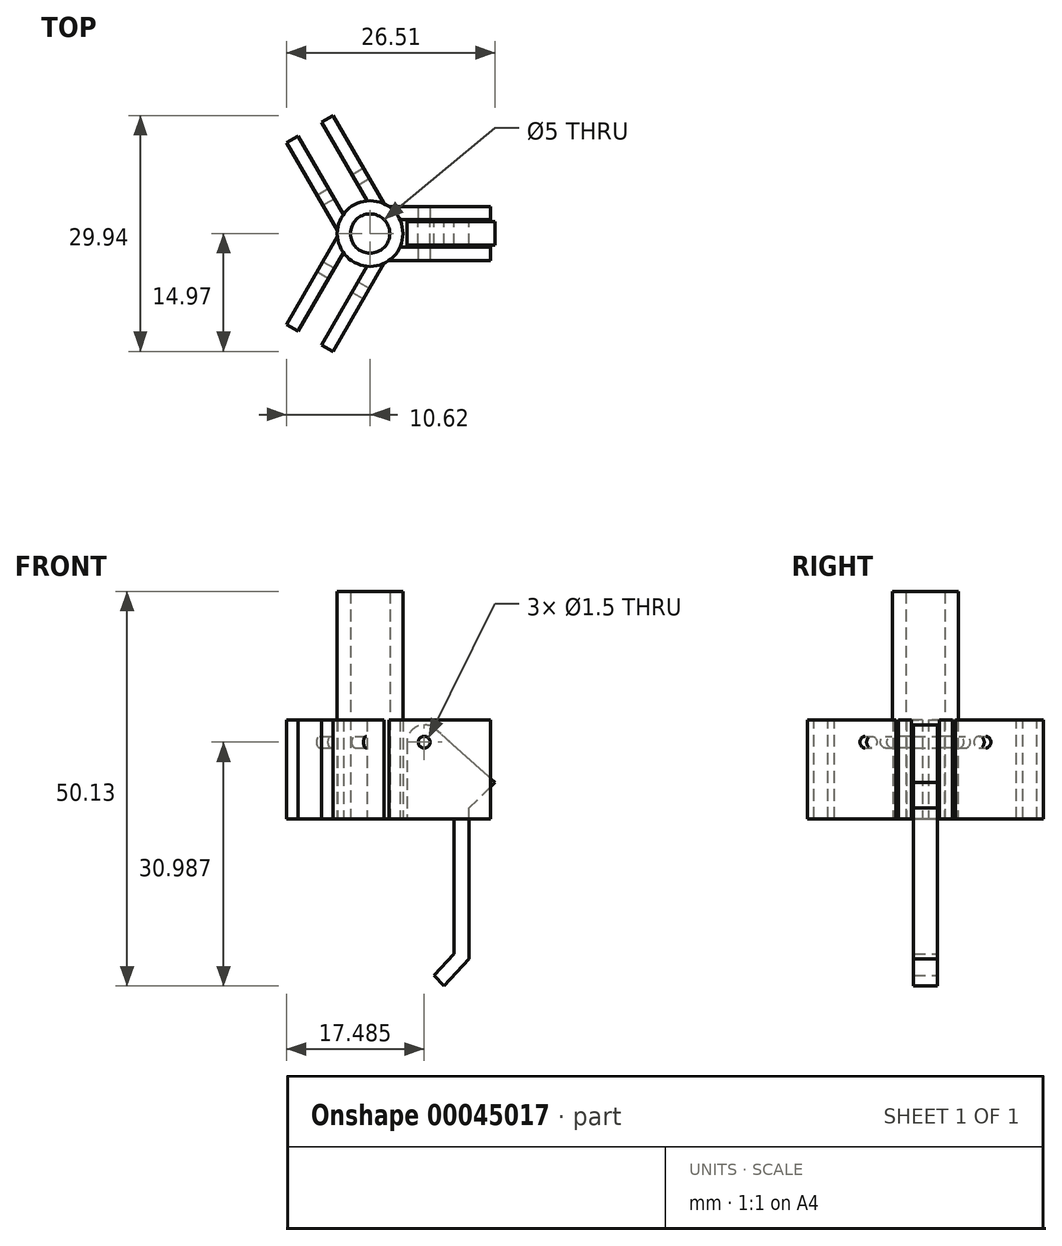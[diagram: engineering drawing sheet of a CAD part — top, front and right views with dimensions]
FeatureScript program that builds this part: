
annotation { "Feature Type Name" : "Feature", "Feature Type Description" : "" }
export const myFeature = defineFeature(function(context is Context, id is Id, definition is map)
    precondition{}
    {
        {
            var Q0;
            Q0=qCreatedBy(makeId("Front.planeOp"),FACE);
            var sketch = newSketch(context, id + "F0", { "sketchPlane" : qUnion([Q0])});
            skLineSegment(sketch, "E0", {"start": v(0, 0) * mm, "end": v(0, 28.9) * mm, "construction": true});
            skLineSegment(sketch, "E1", {"start": v(2.5, 0) * mm, "end": v(2.5, 28.9) * mm});
            skLineSegment(sketch, "E2", {"start": v(4.17, 28.9) * mm, "end": v(4.17, 0) * mm});
            skCircle(sketch, "E3", {"center": v(6.86, 9.76) * mm, "radius": 2.2 * mm});
            skLineSegment(sketch, "E4", {"start": v(4.67, 9.76) * mm, "end": v(4.67, 0) * mm});
            skLineSegment(sketch, "E5", {"start": v(4.67, 0) * mm, "end": v(10.64, 0) * mm});
            skLineSegment(sketch, "E6", {"start": v(10.64, 0) * mm, "end": v(10.64, -17.12) * mm});
            skLineSegment(sketch, "E7", {"start": v(10.64, -17.12) * mm, "end": v(8.14, -19.9) * mm});
            skLineSegment(sketch, "E8", {"start": v(8.14, -19.9) * mm, "end": v(9.42, -21.23) * mm});
            skLineSegment(sketch, "E9", {"start": v(9.42, -21.23) * mm, "end": v(12.55, -17.75) * mm});
            skLineSegment(sketch, "E10", {"start": v(12.55, -17.75) * mm, "end": v(12.55, 1.37) * mm});
            skLineSegment(sketch, "E11", {"start": v(12.55, 1.37) * mm, "end": v(15.89, 4.65) * mm});
            skLineSegment(sketch, "E12", {"start": v(15.89, 4.65) * mm, "end": v(8.33, 11.4) * mm});
            skLineSegment(sketch, "E13", {"start": v(2.5, 28.9) * mm, "end": v(4.17, 28.9) * mm});
            skLineSegment(sketch, "E14", {"start": v(4.17, 0) * mm, "end": v(2.5, 0) * mm});
            skCircle(sketch, "E15", {"center": v(6.86, 9.76) * mm, "radius": 0.75 * mm});
            skSolve(sketch);
        }
        {
            var Q0;
            {var subQ1=sQuery(id+"F0.wireOp",EDGE,"E4");Q0=makeQuery(id+"F0.imprint","IMPRINT",FACE,{"disambiguationData":[TD([[makeQuery(id+"F0.imprint","IMPRINT",EDGE,{"derivedFrom":subQ1}),1.0]])]});}
            var Q1;
            {var subQ0=sQuery(id+"F0.wireOp",EDGE,"E3");var subQ1=makeQuery(id+"F0.imprint","INTERSECT",VERTEX,{"derivedFrom":[subQ0,sQuery(id+"F0.wireOp",EDGE,"E4")]});Q1=makeQuery(id+"F0.imprint","IMPRINT",FACE,{"disambiguationData":[TD([[makeQuery(id+"F0.imprint","IMPRINT",EDGE,{"disambiguationData":[TD([[subQ1,1.0]])],"derivedFrom":subQ0}),1.0]])]});}
            extrude(context, id + "F1", {"entities" : qUnion([Q0, Q1]), "endBound" : BoundingType.SYMMETRIC, "depth" : 3 * mm});
        }
        {
            var Q0;
            Q0=makeQuery(id+"F0.imprint","IMPRINT",FACE,{"disambiguationData":[TD([[makeQuery(id+"F0.imprint","IMPRINT",EDGE,{"derivedFrom":sQuery(id+"F0.wireOp",EDGE,"E1")}),-1.0]])]});
            var Q1;
            Q1=sQuery(id+"F0.wireOp",EDGE,"E0");
            revolve(context, id + "F2", {"entities" : qUnion([Q0]), "axis" : qUnion([Q1]), "revolveType" : RevolveType.FULL});
        }
        {
            var Q0;
            Q0=qCreatedBy(makeId("Right.planeOp"),FACE);
            var sketch = newSketch(context, id + "F3", { "sketchPlane" : qUnion([Q0])});
            skLineSegment(sketch, "E16.bottom", {"start": v(-3.42, 0) * mm, "end": v(-1.75, 0) * mm});
            skLineSegment(sketch, "E16.top", {"start": v(-3.42, 12.6) * mm, "end": v(-1.75, 12.6) * mm});
            skLineSegment(sketch, "E16.left", {"start": v(-3.42, 0) * mm, "end": v(-3.42, 12.6) * mm});
            skLineSegment(sketch, "E16.right", {"start": v(-1.75, 0) * mm, "end": v(-1.75, 12.6) * mm});
            skLineSegment(sketch, "E17.MirrorCS", {"start": v(1.75, 0) * mm, "end": v(1.75, 12.6) * mm});
            skLineSegment(sketch, "E18.MirrorCS", {"start": v(3.42, 12.6) * mm, "end": v(1.75, 12.6) * mm});
            skLineSegment(sketch, "E19.MirrorCS", {"start": v(3.42, 0) * mm, "end": v(3.42, 12.6) * mm});
            skLineSegment(sketch, "E20.MirrorCS", {"start": v(3.42, 0) * mm, "end": v(1.75, 0) * mm});
            skSolve(sketch);
        }
        {
            var Q0;
            Q0=makeQuery(id+"F3.imprint","IMPRINT",FACE,{"disambiguationData":[TD([[makeQuery(id+"F3.imprint","IMPRINT",EDGE,{"derivedFrom":sQuery(id+"F3.wireOp",EDGE,"E17.MirrorCS")}),-1.0]])]});
            var Q1;
            Q1=makeQuery(id+"F3.imprint","IMPRINT",FACE,{"disambiguationData":[TD([[makeQuery(id+"F3.imprint","IMPRINT",EDGE,{"derivedFrom":sQuery(id+"F3.wireOp",EDGE,"E16.bottom")}),1.0]])]});
            extrude(context, id + "F4", {"entities" : qUnion([Q0, Q1]), "depth" : 15.32 * mm, "hasSecondDirection" : true, "secondDirectionOppositeDirection" : false, "secondDirectionDepth" : 2.03 * mm});
        }
        {
            var Q0;
            Q0=makeQuery(id+"F0.imprint","IMPRINT",FACE,{"disambiguationData":[TD([[makeQuery(id+"F0.imprint","IMPRINT",EDGE,{"derivedFrom":sQuery(id+"F0.wireOp",EDGE,"E15")}),1.0]])]});
            extrude(context, id + "F5", {"entities" : qUnion([Q0]), "operationType" : NewBodyOperationType.REMOVE, "endBound" : BoundingType.THROUGH_ALL, "oppositeDirection" : true, "depth" : 25 * mm, "hasSecondDirection" : true, "secondDirectionBound" : SecondDirectionBoundingType.THROUGH_ALL, "secondDirectionOppositeDirection" : false, "secondDirectionDepth" : 25 * mm});
        }
        {
            var Q0;
            Q0=makeQuery(id+"F4.opExtrude","SWEPT_BODY",BODY,{"disambiguationData":[OSD([sQuery(id+"F3.wireOp",EDGE,"E16.bottom"),sQuery(id+"F3.wireOp",EDGE,"E16.top"),sQuery(id+"F3.wireOp",EDGE,"E16.left"),sQuery(id+"F3.wireOp",EDGE,"E16.right")])]});
            var Q1;
            Q1=makeQuery(id+"F4.opExtrude","SWEPT_BODY",BODY,{"disambiguationData":[OSD([sQuery(id+"F3.wireOp",EDGE,"E17.MirrorCS"),sQuery(id+"F3.wireOp",EDGE,"E18.MirrorCS"),sQuery(id+"F3.wireOp",EDGE,"E19.MirrorCS"),sQuery(id+"F3.wireOp",EDGE,"E20.MirrorCS")])]});
            var Q2;
            Q2=sQuery(id+"F0.wireOp",EDGE,"E0");
            circularPattern(context, id + "F6", {"operationType" : NewBodyOperationType.ADD, "entities" : qUnion([Q0, Q1]), "axis" : qUnion([Q2]), "angle" : 120 * degree, "instanceCount" : 3});
        }
    });
